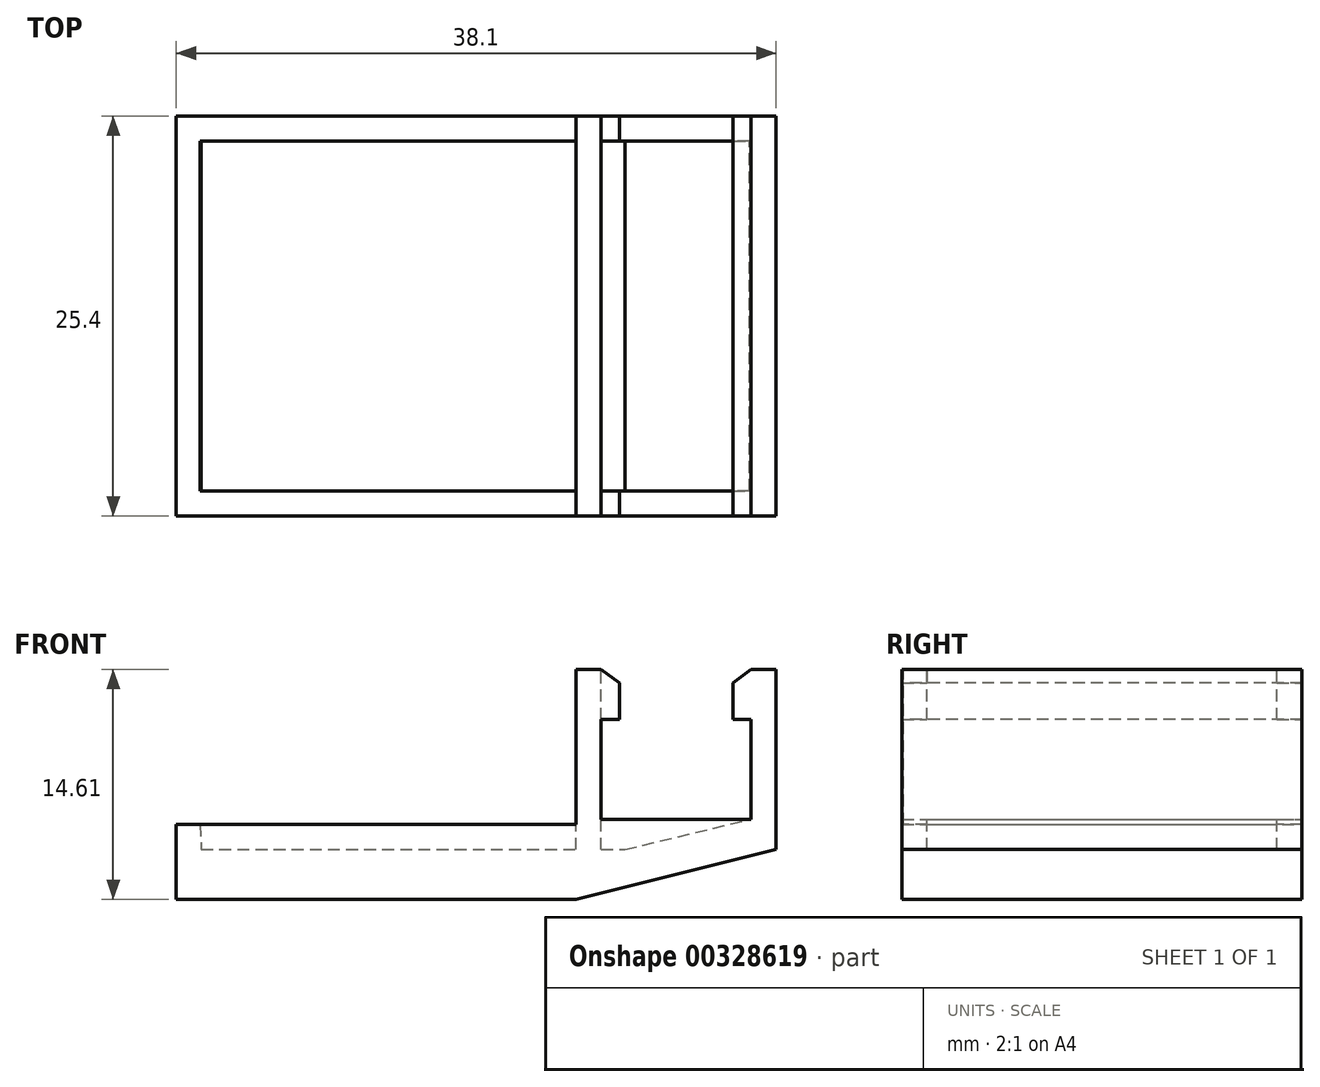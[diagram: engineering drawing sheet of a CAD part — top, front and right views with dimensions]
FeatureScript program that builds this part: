
annotation { "Feature Type Name" : "Feature", "Feature Type Description" : "" }
export const myFeature = defineFeature(function(context is Context, id is Id, definition is map)
    precondition{}
    {
        {
            var Q0;
            Q0=qCreatedBy(makeId("Front.planeOp"),FACE);
            var sketch = newSketch(context, id + "F0", { "sketchPlane" : qUnion([Q0])});
            skLineSegment(sketch, "E0", {"start": v(0, 0) * mm, "end": v(25.4, 0) * mm});
            skLineSegment(sketch, "E1", {"start": v(25.4, 0) * mm, "end": v(38.1, 3.18) * mm});
            skLineSegment(sketch, "E2", {"start": v(38.1, 3.18) * mm, "end": v(38.1, 14.6) * mm});
            skLineSegment(sketch, "E3", {"start": v(38.1, 14.6) * mm, "end": v(36.51, 14.6) * mm});
            skLineSegment(sketch, "E4", {"start": v(34.92, 11.43) * mm, "end": v(36.51, 11.43) * mm});
            skLineSegment(sketch, "E5", {"start": v(36.51, 11.43) * mm, "end": v(36.51, 5.08) * mm});
            skLineSegment(sketch, "E6", {"start": v(36.51, 5.08) * mm, "end": v(26.99, 5.08) * mm});
            skLineSegment(sketch, "E7", {"start": v(26.99, 5.08) * mm, "end": v(26.99, 11.43) * mm});
            skLineSegment(sketch, "E8", {"start": v(26.99, 11.43) * mm, "end": v(28.58, 11.43) * mm});
            skLineSegment(sketch, "E9", {"start": v(28.58, 11.43) * mm, "end": v(28.58, 13.44) * mm});
            skLineSegment(sketch, "E10", {"start": v(28.58, 13.44) * mm, "end": v(26.99, 14.6) * mm});
            skLineSegment(sketch, "E11", {"start": v(26.99, 14.6) * mm, "end": v(25.4, 14.6) * mm});
            skLineSegment(sketch, "E12", {"start": v(25.4, 14.6) * mm, "end": v(25.4, 9.32) * mm});
            skLineSegment(sketch, "E13", {"start": v(25.4, 9.32) * mm, "end": v(25.4, 3.18) * mm});
            skLineSegment(sketch, "E14", {"start": v(25.4, 3.18) * mm, "end": v(0, 3.18) * mm});
            skLineSegment(sketch, "E15", {"start": v(0, 3.18) * mm, "end": v(0, 0) * mm});
            skLineSegment(sketch, "E16", {"start": v(34.92, 11.43) * mm, "end": v(34.92, 13.44) * mm});
            skLineSegment(sketch, "E17", {"start": v(34.92, 13.44) * mm, "end": v(36.51, 14.6) * mm});
            skSolve(sketch);
        }
        {
            var Q0;
            Q0 = qSketchRegion(id + "F0", true);
            extrude(context, id + "F1", {"entities" : qUnion([Q0]), "depth" : 25.4 * mm});
        }
        {
            var Q0;
            Q0=makeQuery(id+"F1.opExtrude","SWEPT_FACE",FACE,{"disambiguationData":[OSD([sQuery(id+"F0.wireOp",EDGE,"E14")])]});
            var sketch = newSketch(context, id + "F2", { "sketchPlane" : qUnion([Q0])});
            skLineSegment(sketch, "E18.bottom", {"start": v(1.59, -1.59) * mm, "end": v(23.81, -1.59) * mm});
            skLineSegment(sketch, "E18.top", {"start": v(1.59, -23.81) * mm, "end": v(23.81, -23.81) * mm});
            skLineSegment(sketch, "E18.left", {"start": v(1.59, -1.59) * mm, "end": v(1.59, -23.81) * mm});
            skLineSegment(sketch, "E18.right", {"start": v(23.81, -1.59) * mm, "end": v(23.81, -23.81) * mm});
            skLineSegment(sketch, "E19.0.0", {"start": v(25.4, 0) * mm, "end": v(0, 0) * mm});
            skLineSegment(sketch, "E19.0.1", {"start": v(0, 0) * mm, "end": v(0, -25.4) * mm});
            skLineSegment(sketch, "E19.0.2", {"start": v(0, -25.4) * mm, "end": v(25.4, -25.4) * mm});
            skLineSegment(sketch, "E19.0.3", {"start": v(25.4, -25.4) * mm, "end": v(25.4, 0) * mm});
            skSolve(sketch);
        }
        {
            var Q0;
            Q0 = qSketchRegion(id + "F2", true);
            extrude(context, id + "F3", {"entities" : qUnion([Q0]), "operationType" : NewBodyOperationType.ADD, "depth" : 1.59 * mm});
        }
        {
            var Q0;
            Q0=makeQuery(id+"F3.opExtrude","SWEPT_FACE",FACE,{"disambiguationData":[OSD([sQuery(id+"F2.wireOp",EDGE,"E18.bottom")])]});
            var sketch = newSketch(context, id + "F4", { "sketchPlane" : qUnion([Q0])});
            skLineSegment(sketch, "E20", {"start": v(1.4, 8.1) * mm, "end": v(1.59, 3.18) * mm});
            skLineSegment(sketch, "E21", {"start": v(1.59, 3.18) * mm, "end": v(28.5, 3.18) * mm});
            skLineSegment(sketch, "E22", {"start": v(28.5, 3.17) * mm, "end": v(36.44, 5.09) * mm});
            skLineSegment(sketch, "E23", {"start": v(36.44, 5.09) * mm, "end": v(32.87, 15.34) * mm});
            skLineSegment(sketch, "E24", {"start": v(32.87, 15.34) * mm, "end": v(5.73, 17.78) * mm});
            skLineSegment(sketch, "E25", {"start": v(5.73, 17.78) * mm, "end": v(1.4, 8.1) * mm});
            skSolve(sketch);
        }
        {
            var Q0;
            Q0 = qSketchRegion(id + "F4", true);
            var Q1;
            Q1=makeQuery(id+"F3.opExtrude","SWEPT_FACE",FACE,{"disambiguationData":[OSD([sQuery(id+"F2.wireOp",EDGE,"E18.top")])]});
            extrude(context, id + "F5", {"entities" : qUnion([Q0]), "operationType" : NewBodyOperationType.REMOVE, "endBound" : BoundingType.UP_TO_SURFACE, "endBoundEntityFace" : qUnion([Q1]), "depth" : 25.4 * mm});
        }
        {
            var Q0;
            {var subQ3=sQuery(id+"F0.wireOp",EDGE,"E11");Q0=makeQuery(id+"F5.boolean.opBoolean","SPLIT",FACE,{"disambiguationData":[TD([makeQuery(id+"F3.opExtrude","SWEPT_FACE",FACE,{"disambiguationData":[OSD([sQuery(id+"F2.wireOp",EDGE,"E18.bottom")])]})])],"derivedFrom":makeQuery(id+"F1.opExtrude","SWEPT_FACE",FACE,{"disambiguationData":[OSD([subQ3])]})});}
            var sketch = newSketch(context, id + "F6", { "sketchPlane" : qUnion([Q0])});
            skLineSegment(sketch, "E26.bottom", {"start": v(26.99, 0) * mm, "end": v(23.18, 0) * mm});
            skLineSegment(sketch, "E26.top", {"start": v(26.99, -1.59) * mm, "end": v(23.18, -1.59) * mm});
            skLineSegment(sketch, "E26.left", {"start": v(26.99, 0) * mm, "end": v(26.99, -1.59) * mm});
            skLineSegment(sketch, "E26.right", {"start": v(23.18, 0) * mm, "end": v(23.18, -1.59) * mm});
            skLineSegment(sketch, "E27.bottom", {"start": v(26.99, -23.81) * mm, "end": v(20.64, -23.81) * mm});
            skLineSegment(sketch, "E27.top", {"start": v(26.99, -25.4) * mm, "end": v(20.64, -25.4) * mm});
            skLineSegment(sketch, "E27.left", {"start": v(26.99, -23.81) * mm, "end": v(26.99, -25.4) * mm});
            skLineSegment(sketch, "E27.right", {"start": v(20.64, -23.81) * mm, "end": v(20.64, -25.4) * mm});
            skSolve(sketch);
        }
        {
            var Q0;
            Q0=makeQuery(id+"F3.boolean.opBoolean","MERGE",FACE,{"derivedFrom":[makeQuery(id+"F1.opExtrude","CAP_FACE",FACE,{"disambiguationData":[OSD([sQuery(id+"F0.wireOp",EDGE,"E0"),sQuery(id+"F0.wireOp",EDGE,"E1"),sQuery(id+"F0.wireOp",EDGE,"E2"),sQuery(id+"F0.wireOp",EDGE,"E3"),sQuery(id+"F0.wireOp",EDGE,"E4"),sQuery(id+"F0.wireOp",EDGE,"E5"),sQuery(id+"F0.wireOp",EDGE,"E6"),sQuery(id+"F0.wireOp",EDGE,"E7"),sQuery(id+"F0.wireOp",EDGE,"E8"),sQuery(id+"F0.wireOp",EDGE,"E9"),sQuery(id+"F0.wireOp",EDGE,"E10"),sQuery(id+"F0.wireOp",EDGE,"E11"),sQuery(id+"F0.wireOp",EDGE,"E12"),sQuery(id+"F0.wireOp",EDGE,"E13"),sQuery(id+"F0.wireOp",EDGE,"E14"),sQuery(id+"F0.wireOp",EDGE,"E15"),sQuery(id+"F0.wireOp",EDGE,"E16"),sQuery(id+"F0.wireOp",EDGE,"E17")])],"isStart":false}),makeQuery(id+"F3.opExtrude","SWEPT_FACE",FACE,{"disambiguationData":[OSD([sQuery(id+"F2.wireOp",EDGE,"E19.0.2")])]})]});
            var sketch = newSketch(context, id + "F7", { "sketchPlane" : qUnion([Q0])});
            skSolve(sketch);
        }
        {
            var Q0;
            Q0=makeQuery(id+"F7.imprint","IMPRINT",FACE,{"disambiguationData":[TD([[makeQuery(id+"F7.imprint","IMPRINT",EDGE,{"derivedFrom":makeQuery(id+"F1.opExtrude","CAP_EDGE",EDGE,{"disambiguationData":[OSD([sQuery(id+"F0.wireOp",EDGE,"E0")])],"isStart":false})}),1.0]])]});
            var sketch = newSketch(context, id + "F8", { "sketchPlane" : qUnion([Q0])});
            skLineSegment(sketch, "E28.bottom", {"start": v(28.15, 14.28) * mm, "end": v(35.36, 14.28) * mm});
            skLineSegment(sketch, "E28.top", {"start": v(28.15, 10.15) * mm, "end": v(35.36, 10.15) * mm});
            skLineSegment(sketch, "E28.left", {"start": v(28.15, 14.28) * mm, "end": v(28.15, 10.15) * mm});
            skLineSegment(sketch, "E28.right", {"start": v(35.36, 14.28) * mm, "end": v(35.36, 10.15) * mm});
            skSolve(sketch);
        }
        {
            var Q0;
            Q0 = qSketchRegion(id + "F8", true);
            extrude(context, id + "F9", {"entities" : qUnion([Q0]), "operationType" : NewBodyOperationType.REMOVE, "oppositeDirection" : true, "depth" : 25.4 * mm});
        }
        {
            var Q0;
            {var subQ0=sQuery(id+"F6.wireOp",EDGE,"E26.left");Q0=makeQuery(id+"F6.imprint","IMPRINT",FACE,{"disambiguationData":[TD([[makeQuery(id+"F6.imprint","IMPRINT",EDGE,{"derivedFrom":subQ0}),1.0]])]});}
            var sketch = newSketch(context, id + "F10", { "sketchPlane" : qUnion([Q0])});
            skLineSegment(sketch, "E29.bottom", {"start": v(27, 0) * mm, "end": v(25.38, 0) * mm});
            skLineSegment(sketch, "E29.top", {"start": v(27, -25.3) * mm, "end": v(25.38, -25.3) * mm});
            skLineSegment(sketch, "E29.left", {"start": v(27, 0) * mm, "end": v(27, -25.3) * mm});
            skLineSegment(sketch, "E29.right", {"start": v(25.38, 0) * mm, "end": v(25.38, -25.3) * mm});
            skSolve(sketch);
        }
        {
            var Q0;
            Q0 = qSketchRegion(id + "F10", true);
            var Q1;
            Q1=makeQuery(id+"F5.boolean.opBoolean","MERGE",FACE,{"derivedFrom":[makeQuery(id+"F1.opExtrude","SWEPT_FACE",FACE,{"disambiguationData":[OSD([sQuery(id+"F0.wireOp",EDGE,"E14")])]}),makeQuery(id+"F5.opExtrude","SWEPT_FACE",FACE,{"disambiguationData":[OSD([sQuery(id+"F4.wireOp",EDGE,"E21")])]})]});
            extrude(context, id + "F11", {"entities" : qUnion([Q0]), "operationType" : NewBodyOperationType.ADD, "endBound" : BoundingType.UP_TO_SURFACE, "oppositeDirection" : true, "endBoundEntityFace" : qUnion([Q1]), "depth" : 25.4 * mm});
        }
    });
